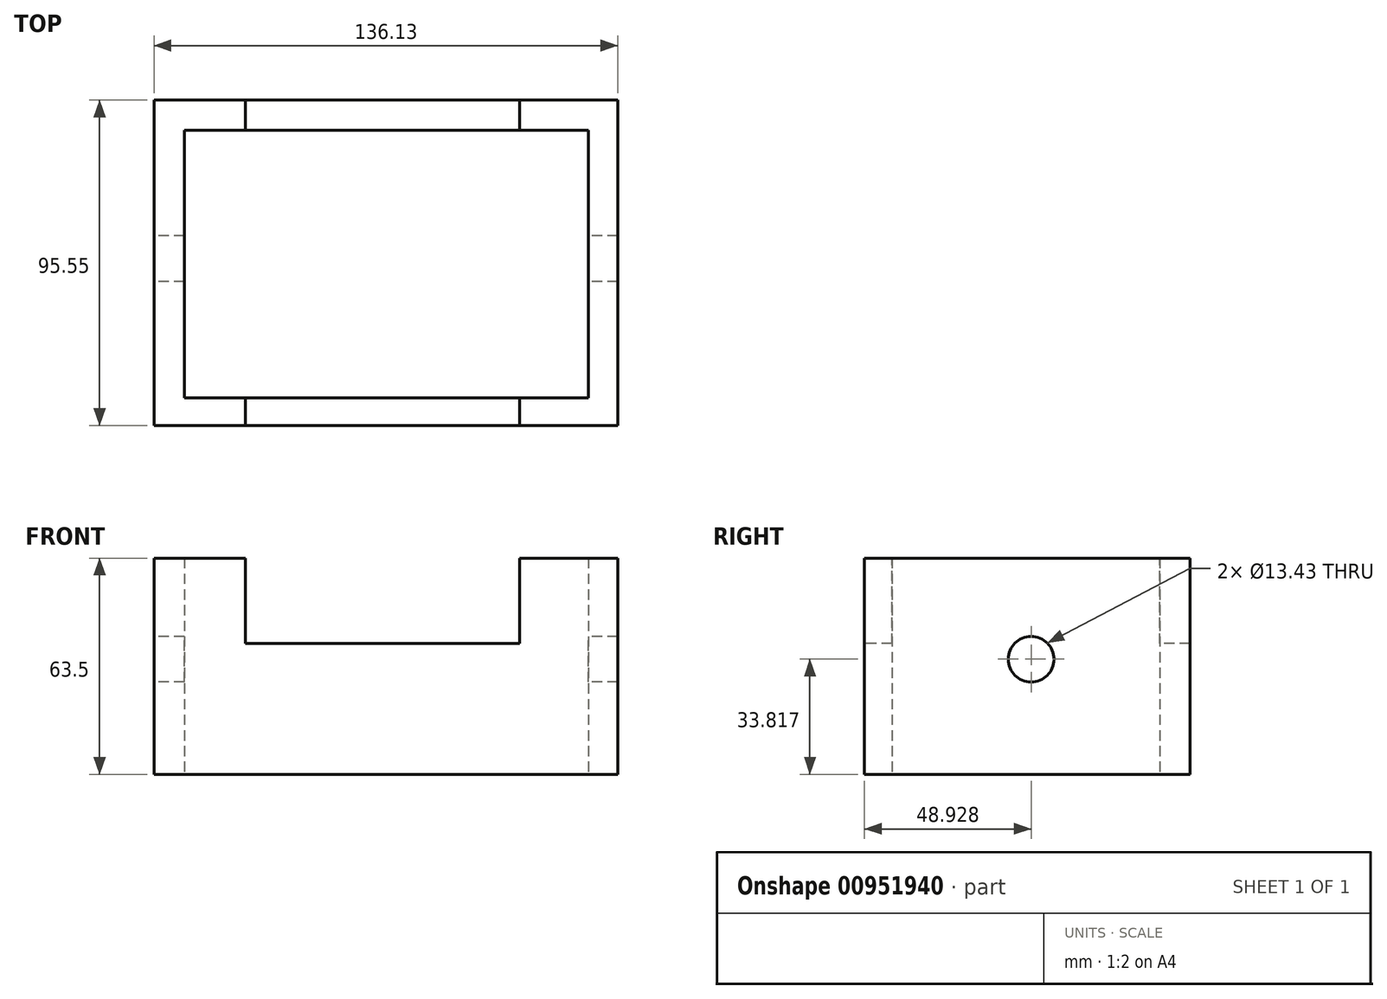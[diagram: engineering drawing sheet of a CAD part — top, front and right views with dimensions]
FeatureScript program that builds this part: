
annotation { "Feature Type Name" : "Feature", "Feature Type Description" : "" }
export const myFeature = defineFeature(function(context is Context, id is Id, definition is map)
    precondition{}
    {
        {
            var Q0;
            Q0=qCreatedBy(makeId("Top.planeOp"),FACE);
            var sketch = newSketch(context, id + "F0", { "sketchPlane" : qUnion([Q0])});
            skLineSegment(sketch, "E0.bottom", {"start": v(-67.2, 50.22) * mm, "end": v(68.93, 50.22) * mm});
            skLineSegment(sketch, "E0.top", {"start": v(-67.2, -45.33) * mm, "end": v(68.93, -45.33) * mm});
            skLineSegment(sketch, "E0.left", {"start": v(-67.2, 50.22) * mm, "end": v(-67.2, -45.33) * mm});
            skLineSegment(sketch, "E0.right", {"start": v(68.93, 50.22) * mm, "end": v(68.93, -45.33) * mm});
            skLineSegment(sketch, "E1.bottom", {"start": v(-58.28, 41.3) * mm, "end": v(60.3, 41.3) * mm});
            skLineSegment(sketch, "E1.top", {"start": v(-58.28, -37.27) * mm, "end": v(60.3, -37.27) * mm});
            skLineSegment(sketch, "E1.left", {"start": v(-58.28, 41.3) * mm, "end": v(-58.28, -37.27) * mm});
            skLineSegment(sketch, "E1.right", {"start": v(60.3, 41.3) * mm, "end": v(60.3, -37.27) * mm});
            skSolve(sketch);
        }
        {
            var Q0;
            Q0=makeQuery(id+"F0.imprint","IMPRINT",FACE,{"disambiguationData":[TD([[makeQuery(id+"F0.imprint","IMPRINT",EDGE,{"derivedFrom":sQuery(id+"F0.wireOp",EDGE,"E0.bottom")}),-1.0]])]});
            extrude(context, id + "F1", {"entities" : qUnion([Q0]), "depth" : 63.5 * mm, "offsetDistance" : 25.4 * mm});
        }
        {
            var Q0;
            Q0=makeQuery(id+"F1.opExtrude","SWEPT_FACE",FACE,{"disambiguationData":[OSD([sQuery(id+"F0.wireOp",EDGE,"E0.top")])]});
            var sketch = newSketch(context, id + "F2", { "sketchPlane" : qUnion([Q0])});
            skLineSegment(sketch, "E2.bottom", {"start": v(-40.44, 63.5) * mm, "end": v(40.15, 63.5) * mm});
            skLineSegment(sketch, "E2.top", {"start": v(-40.44, 38.42) * mm, "end": v(40.15, 38.42) * mm});
            skLineSegment(sketch, "E2.left", {"start": v(-40.44, 63.5) * mm, "end": v(-40.44, 38.42) * mm});
            skLineSegment(sketch, "E2.right", {"start": v(40.15, 63.5) * mm, "end": v(40.15, 38.42) * mm});
            skSolve(sketch);
        }
        {
            var Q0;
            Q0=makeQuery(id+"F2.imprint","IMPRINT",FACE,{"disambiguationData":[TD([[makeQuery(id+"F2.imprint","IMPRINT",EDGE,{"derivedFrom":sQuery(id+"F2.wireOp",EDGE,"E2.bottom")}),-1.0]])]});
            extrude(context, id + "F3", {"entities" : qUnion([Q0]), "operationType" : NewBodyOperationType.REMOVE, "oppositeDirection" : true, "depth" : 142 * mm, "offsetDistance" : 25.4 * mm});
        }
        {
            var Q0;
            Q0=makeQuery(id+"F1.opExtrude","SWEPT_FACE",FACE,{"disambiguationData":[OSD([sQuery(id+"F0.wireOp",EDGE,"E0.left")])]});
            var sketch = newSketch(context, id + "F4", { "sketchPlane" : qUnion([Q0])});
            skCircle(sketch, "E3", {"center": v(-3.6, 33.82) * mm, "radius": 6.71 * mm});
            skSolve(sketch);
        }
        {
            var Q0;
            Q0=makeQuery(id+"F4.imprint","IMPRINT",FACE,{"disambiguationData":[TD([[makeQuery(id+"F4.imprint","IMPRINT",EDGE,{"derivedFrom":sQuery(id+"F4.wireOp",EDGE,"E3")}),1.0]])]});
            extrude(context, id + "F5", {"entities" : qUnion([Q0]), "operationType" : NewBodyOperationType.REMOVE, "oppositeDirection" : true, "depth" : 186.7 * mm, "offsetDistance" : 25.4 * mm});
        }
    });
